# Revit family: Rohrschelle Maxima PSM, M16, Ø106-129, o.D
name_source: partatom
category: HLS-Bauteile
revit_build: Autodesk Revit 2017 (Build: 20190507_1515(x64)
units: mm (PartAtom-declared; Revit-internal decimal feet)

## family parameters
Arbeitsebenenbasiert = Ja
Beim Laden mit Abzugskörper schneiden = Nein
Bemaßung runder Anschluss = Durchmesser verwenden
Gemeinsam genutzt = Ja
Immer vertikal = Nein
Raumberechnungspunkt = Nein
Teiletyp = Normal

## types (4) — shared parameters
A = 13 mm
Anschluss = M16
Anschlußhöhe = 23 mm
Bauart = zweiteilig
Brandschutz = RAL-GZ 656
DF1 = 26 mm
DF2 = 28 mm  [stored 0.0918635 ft]
DVS = 15 mm  [stored 0.0492126 ft]
Fabrikat = MEFA
Firma = MEFA Befestigungs- und Montagesysteme GmbH
HGA = 10 mm  [stored 0.0328084 ft]
Kurztext1 = Rohrschelle Maxima PSM 30x3,0
MB = 30 mm  [stored 0.0984252 ft]
MD = 3 mm  [stored 0.00984252 ft]
Material = Stahl
Materialmaße = 30x3,0 mm
Materialname = S235
Mengeneinheit = St
Oberflaeche = galvanisch verzinkt
Verschluss = Pendelsteckmuttern
Verschluss-Schraube = M8
Vorgabe-Ansicht = 1219 mm
max. zul. Last = 4.00 kN
max. zul. Last horizontal = 0.00 kN
max. zul. Last vertikal = 0.00 kN
vpe = 1 St
zero-valued in all types: Nennweite DN Rohr, Rohraußendurchmesser, Stärke Material

## per-type parameters (varying)
| type | AB | Achsabstand | Artikelnummer | B | Breite | D | Dmax | Dmin | EAN | Gewicht | Gewicht pro Bauteil | H | Kurztext2 | R | RM | Rohraußendurchmesser Zoll | S | max. Höhe | max. Rohraußendurchmesser | min. Rohraußendurchmesser |
| Maxima PSM, M16, Ø106-112, o.D | 6 mm  [stored 0.019685 ft] | 146 mm | 008160701 | 172 mm  [stored 0.564304 ft] | 172 mm  [stored 0.564304 ft] | 112 mm  [stored 0.367454 ft] | 112 mm  [stored 0.367454 ft] | 106 mm  [stored 0.347769 ft] | 4250928455116 | 0.41 kg | 0.41 kg | 128 mm  [stored 0.419948 ft] | 106 - 112 mm M16 | 56 mm  [stored 0.183727 ft] | 59 mm | Zoll | 146 mm  [stored 0.479003 ft] | 138 mm  [stored 0.452756 ft] | 112 mm  [stored 0.367454 ft] | 106 mm  [stored 0.347769 ft] |
| Maxima PSM, M16, Ø114-118, o.D | 4 mm  [stored 0.0131234 ft] | 152 mm | 008162101 | 178 mm  [stored 0.58399 ft] | 178 mm  [stored 0.58399 ft] | 118 mm | 118 mm | 114 mm  [stored 0.374016 ft] | 4250928455123 | 0.43 kg | 0.43 kg | 134 mm | 114 - 118 mm M16 | 59 mm | 62 mm  [stored 0.203412 ft] | 4 Zoll | 152 mm | 144 mm  [stored 0.472441 ft] | 118 mm | 114 mm  [stored 0.374016 ft] |
| Maxima PSM, M16, Ø120-124, o.D | 4 mm  [stored 0.0131234 ft] | 158 mm | 008164301 | 184 mm  [stored 0.603675 ft] | 184 mm  [stored 0.603675 ft] | 124 mm  [stored 0.406824 ft] | 124 mm  [stored 0.406824 ft] | 120 mm  [stored 0.393701 ft] | 4250928455130 | 0.45 kg | 0.45 kg | 140 mm  [stored 0.459318 ft] | 120 - 124 mm M16 | 62 mm  [stored 0.203412 ft] | 65 mm  [stored 0.213255 ft] | Zoll | 158 mm | 150 mm | 124 mm  [stored 0.406824 ft] | 120 mm  [stored 0.393701 ft] |
| Maxima PSM, M16, Ø125-129, o.D | 4 mm  [stored 0.0131234 ft] | 163 mm | 008164501 | 189 mm  [stored 0.620079 ft] | 189 mm  [stored 0.620079 ft] | 129 mm  [stored 0.423228 ft] | 129 mm  [stored 0.423228 ft] | 125 mm  [stored 0.410105 ft] | 4250928455154 | 0.46 kg | 0.46 kg | 145 mm  [stored 0.475722 ft] | 125 - 129 mm M16 | 65 mm  [stored 0.213255 ft] | 68 mm | Zoll | 163 mm  [stored 0.534777 ft] | 155 mm  [stored 0.50853 ft] | 129 mm  [stored 0.423228 ft] | 125 mm  [stored 0.410105 ft] |

note: [stored X ft] marks values corroborated as IEEE doubles in the binary element streams (Revit-internal decimal feet)

## geometry (parser evidence)
native form markers: Sweep x2
no freeform markers — native parametric forms only
